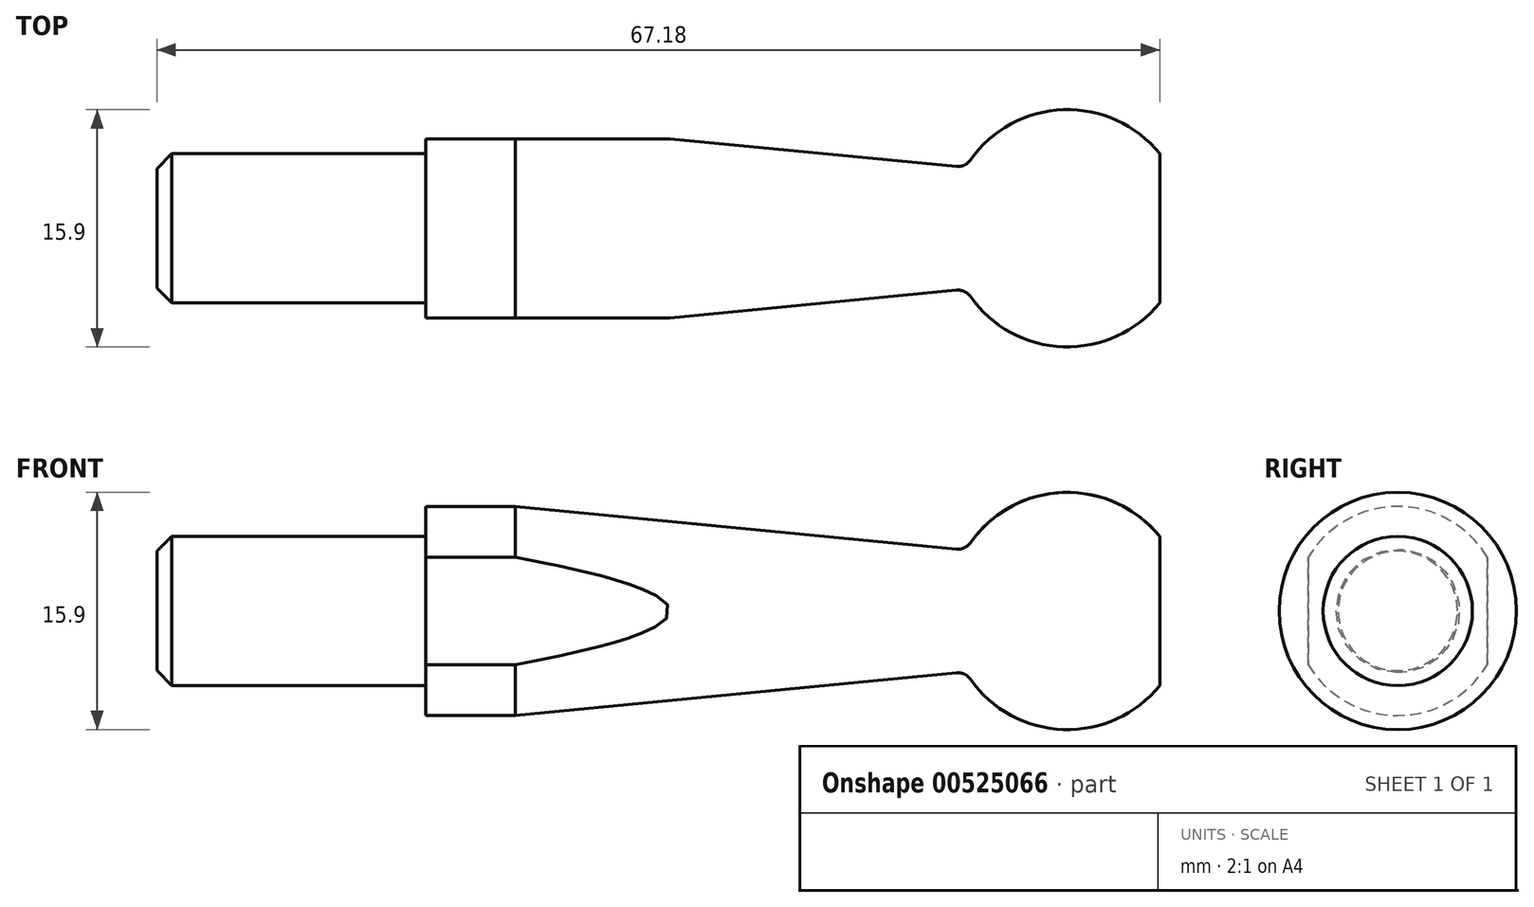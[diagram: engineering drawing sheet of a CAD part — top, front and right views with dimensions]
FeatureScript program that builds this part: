
annotation { "Feature Type Name" : "Feature", "Feature Type Description" : "" }
export const myFeature = defineFeature(function(context is Context, id is Id, definition is map)
    precondition{}
    {
        {
            var Q0;
            Q0=qCreatedBy(makeId("Front.planeOp"),FACE);
            var sketch = newSketch(context, id + "F0", { "sketchPlane" : qUnion([Q0])});
            skArc(sketch, "E0", {"start": v(6.18, 5) * mm, "mid": v(-0.56, 7.93) * mm, "end": v(-6.82, 4.09) * mm});
            skLineSegment(sketch, "E1", {"start": v(-55, 5) * mm, "end": v(-55, 0) * mm, "construction": true});
            skLineSegment(sketch, "E2", {"start": v(-61, 0) * mm, "end": v(6.18, 0) * mm});
            skLineSegment(sketch, "E3", {"start": v(-43, 7) * mm, "end": v(-43, 5) * mm});
            skLineSegment(sketch, "E4", {"start": v(-43, 5) * mm, "end": v(-61, 5) * mm});
            skLineSegment(sketch, "E5", {"start": v(-43, 7) * mm, "end": v(-37, 7) * mm});
            skLineSegment(sketch, "E6", {"start": v(-37, 7) * mm, "end": v(-6.82, 4.09) * mm});
            skLineSegment(sketch, "E7", {"start": v(-61, 0) * mm, "end": v(-61, 5) * mm});
            skLineSegment(sketch, "E8", {"start": v(6.18, 0) * mm, "end": v(6.18, 5) * mm});
            skSolve(sketch);
        }
        {
            var Q0;
            Q0=makeQuery(id+"F0.imprint","IMPRINT",FACE,{"disambiguationData":[TD([[makeQuery(id+"F0.imprint","IMPRINT",EDGE,{"derivedFrom":sQuery(id+"F0.wireOp",EDGE,"E0")}),1.0]])]});
            var Q1;
            Q1=sQuery(id+"F0.wireOp",EDGE,"E2");
            revolve(context, id + "F1", {"entities" : qUnion([Q0]), "axis" : qUnion([Q1]), "revolveType" : RevolveType.FULL});
        }
        {
            var Q0;
            Q0=qCreatedBy(makeId("Top.planeOp"),FACE);
            var sketch = newSketch(context, id + "F2", { "sketchPlane" : qUnion([Q0])});
            skLineSegment(sketch, "E9.bottom", {"start": v(-43, 23.98) * mm, "end": v(-23.95, 23.98) * mm});
            skLineSegment(sketch, "E9.top", {"start": v(-43, 6) * mm, "end": v(-23.95, 6) * mm});
            skLineSegment(sketch, "E9.left", {"start": v(-43, 23.98) * mm, "end": v(-43, 6) * mm});
            skLineSegment(sketch, "E9.right", {"start": v(-23.95, 23.98) * mm, "end": v(-23.95, 6) * mm});
            skLineSegment(sketch, "E10.MirrorCS", {"start": v(-43, -23.98) * mm, "end": v(-43, -6) * mm});
            skLineSegment(sketch, "E11.MirrorCS", {"start": v(-43, -23.98) * mm, "end": v(-23.95, -23.98) * mm});
            skLineSegment(sketch, "E12.MirrorCS", {"start": v(-23.95, -23.98) * mm, "end": v(-23.95, -6) * mm});
            skLineSegment(sketch, "E13.MirrorCS", {"start": v(-43, -6) * mm, "end": v(-23.95, -6) * mm});
            skSolve(sketch);
        }
        {
            var Q0;
            Q0=makeQuery(id+"F2.imprint","IMPRINT",FACE,{"disambiguationData":[TD([[makeQuery(id+"F2.imprint","IMPRINT",EDGE,{"derivedFrom":sQuery(id+"F2.wireOp",EDGE,"E9.bottom")}),-1.0]])]});
            var Q1;
            Q1=makeQuery(id+"F2.imprint","IMPRINT",FACE,{"disambiguationData":[TD([[makeQuery(id+"F2.imprint","IMPRINT",EDGE,{"derivedFrom":sQuery(id+"F2.wireOp",EDGE,"E10.MirrorCS")}),-1.0]])]});
            extrude(context, id + "F3", {"entities" : qUnion([Q0, Q1]), "operationType" : NewBodyOperationType.REMOVE, "endBound" : BoundingType.SYMMETRIC, "oppositeDirection" : true, "depth" : 25.4 * mm, "offsetDistance" : 25.4 * mm});
        }
        {
            var Q0;
            Q0=makeQuery(id+"F1.opRevolve","SWEPT_EDGE",EDGE,{"disambiguationData":[OSD([sQuery(id+"F0.wireOp",EDGE,"E4"),sQuery(id+"F0.wireOp",EDGE,"E7")])]});
            chamfer(context, id + "F4", {"entities" : qUnion([Q0]), "width" : 1 * mm, "tangentPropagation" : true});
        }
        {
            var Q0;
            Q0=makeQuery(id+"F1.opRevolve","SWEPT_EDGE",EDGE,{"disambiguationData":[OSD([sQuery(id+"F0.wireOp",EDGE,"E0"),sQuery(id+"F0.wireOp",EDGE,"E6")])]});
            fillet(context, id + "F5", {"entities" : qUnion([Q0]), "radius" : 1 * mm, "tangentPropagation" : true, "allowEdgeOverflow" : false});
        }
    });
